# Revit family: Furniture_Tables_Svedholm_Aperto
name_source: partatom
category: Furniture
revit_build: Autodesk Revit 2018 (Build: 20190510_1515(x64)
units: mm (PartAtom-declared; Revit-internal decimal feet)

## family parameters
Always vertical = Yes
Cut with Voids When Loaded = No
OmniClass Number = 23.21.23.00
OmniClass Title = Residential Furniture and Equipment
Room Calculation Point = No
Shared = No
Work Plane-Based = Yes

## types (1)
- ART - (310.600.001)
    BIMobject category = Tables
    Default Elevation = 1219 mm
    Description = A side table with table top of tempered glass with ceramic paint. Table base of powder coated steel.
    Edition number = 1
    IFC Classification = Furniture
    Manufacturer = Svedholm
    Manufacturer name = Svedholm
    Model = Aperto
    OmniClass Code = 23-21 23 00
    OmniClass Description = Residential Furniture and Equipment
    Product Guid = 4fdcf742-9a9d-41ce-91be-2ac48571b458
    Product SKU = Aperto
    Product data url = https://bimobject.com
    Product family = Aperto
    Product group = Tables
    Product name = Aperto
    Product url = https://www.svedholm.se
    QR code = https://bimobject.com
    Secondary material = Svedholm - Glass - Transparent
    UNSPSC Code = 56
    URL = https://www.svedholm.se
    Uniclass 1.4 Code = L8221
    Uniclass 1.4 Description = Tables

## geometry (parser evidence)
native form markers: Sweep x4
no freeform markers — native parametric forms only
